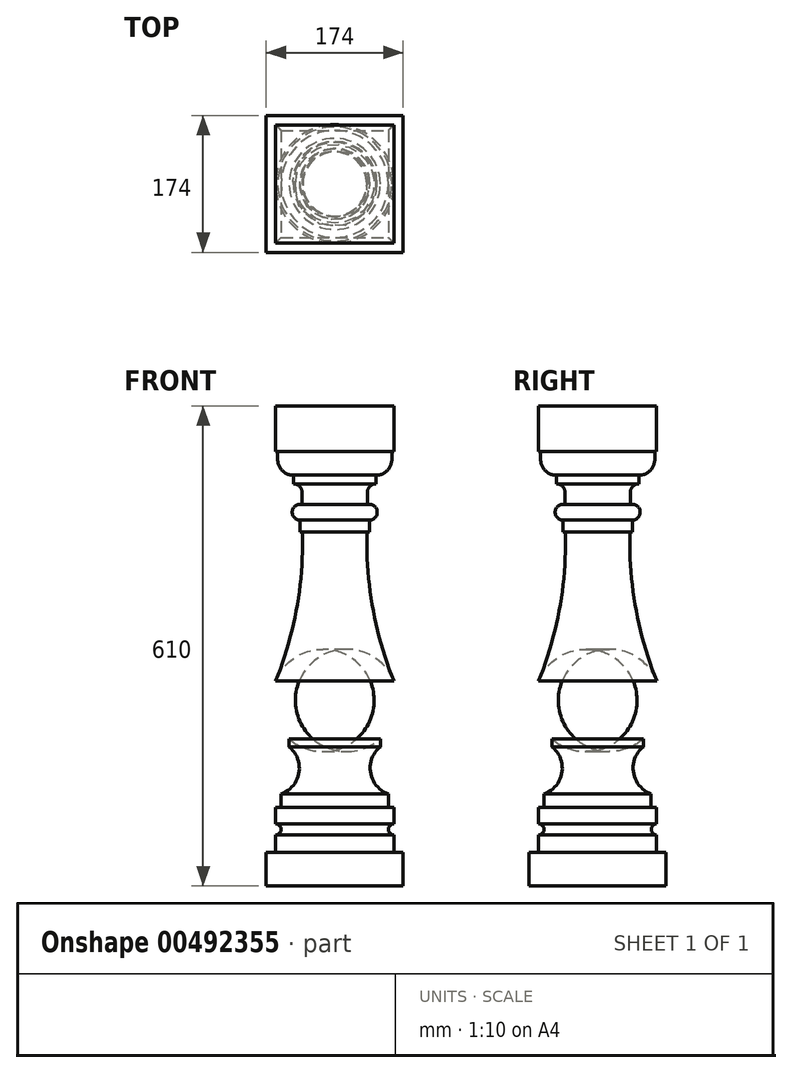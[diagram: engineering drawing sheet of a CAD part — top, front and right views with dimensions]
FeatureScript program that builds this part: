
annotation { "Feature Type Name" : "Feature", "Feature Type Description" : "" }
export const myFeature = defineFeature(function(context is Context, id is Id, definition is map)
    precondition{}
    {
        {
            var Q0;
            Q0=qCreatedBy(makeId("Top.planeOp"),FACE);
            var sketch = newSketch(context, id + "F0", { "sketchPlane" : qUnion([Q0])});
            skLineSegment(sketch, "E0.bottom", {"start": v(87, -87) * mm, "end": v(-87, -87) * mm});
            skLineSegment(sketch, "E0.top", {"start": v(87, 87) * mm, "end": v(-87, 87) * mm});
            skLineSegment(sketch, "E0.left", {"start": v(87, -87) * mm, "end": v(87, 87) * mm});
            skLineSegment(sketch, "E0.right", {"start": v(-87, -87) * mm, "end": v(-87, 87) * mm});
            skPoint(sketch, "E0.middle", {"position": v(0, 0) * mm});
            skSolve(sketch);
        }
        {
            var Q0;
            Q0 = qSketchRegion(id + "F0", true);
            extrude(context, id + "F1", {"entities" : qUnion([Q0]), "depth" : 43 * mm});
        }
        {
            var Q0;
            Q0=makeQuery(id+"F1.opExtrude","CAP_FACE",FACE,{"disambiguationData":[OSD([sQuery(id+"F0.wireOp",EDGE,"E0.bottom"),sQuery(id+"F0.wireOp",EDGE,"E0.top"),sQuery(id+"F0.wireOp",EDGE,"E0.left"),sQuery(id+"F0.wireOp",EDGE,"E0.right")])],"isStart":false});
            var sketch = newSketch(context, id + "F2", { "sketchPlane" : qUnion([Q0])});
            skLineSegment(sketch, "E1.bottom", {"start": v(75, -75) * mm, "end": v(-75, -75) * mm});
            skLineSegment(sketch, "E1.top", {"start": v(75, 75) * mm, "end": v(-75, 75) * mm});
            skLineSegment(sketch, "E1.left", {"start": v(75, -75) * mm, "end": v(75, 75) * mm});
            skLineSegment(sketch, "E1.right", {"start": v(-75, -75) * mm, "end": v(-75, 75) * mm});
            skPoint(sketch, "E1.middle", {"position": v(0, 0) * mm});
            skSolve(sketch);
        }
        {
            var Q0;
            Q0 = qSketchRegion(id + "F2", true);
            extrude(context, id + "F3", {"entities" : qUnion([Q0]), "operationType" : NewBodyOperationType.ADD, "depth" : 57 * mm});
        }
        {
            var Q0;
            Q0=makeQuery(id+"F3.opExtrude","SWEPT_FACE",FACE,{"disambiguationData":[OSD([sQuery(id+"F2.wireOp",EDGE,"E1.bottom")])]});
            var sketch = newSketch(context, id + "F4", { "sketchPlane" : qUnion([Q0])});
            skCircle(sketch, "E2", {"center": v(75, 72) * mm, "radius": 7 * mm});
            skCircle(sketch, "E3", {"center": v(-75, 72) * mm, "radius": 7 * mm});
            skSolve(sketch);
        }
        {
            var Q0;
            Q0 = qSketchRegion(id + "F4", true);
            extrude(context, id + "F5", {"entities" : qUnion([Q0]), "operationType" : NewBodyOperationType.REMOVE, "endBound" : BoundingType.THROUGH_ALL, "oppositeDirection" : true, "depth" : 123 * mm});
        }
        {
            var Q0;
            {var subQ0=sQuery(id+"F2.wireOp",EDGE,"E1.bottom");var subQ1=sQuery(id+"F2.wireOp",EDGE,"E1.left");var subQ2=sQuery(id+"F2.wireOp",EDGE,"E1.top");Q0=makeQuery(id+"F5.boolean.opBoolean","SPLIT",FACE,{"disambiguationData":[TD([makeQuery(id+"F3.opExtrude","CAP_FACE",FACE,{"disambiguationData":[OSD([subQ0,subQ2,subQ1,sQuery(id+"F2.wireOp",EDGE,"E1.right")])],"isStart":false})])],"derivedFrom":makeQuery(id+"F3.opExtrude","SWEPT_FACE",FACE,{"disambiguationData":[OSD([subQ1])]})});}
            var sketch = newSketch(context, id + "F6", { "sketchPlane" : qUnion([Q0])});
            skCircle(sketch, "E4", {"center": v(75, 72) * mm, "radius": 7 * mm});
            skCircle(sketch, "E5", {"center": v(-75, 72) * mm, "radius": 7 * mm});
            skSolve(sketch);
        }
        {
            var Q0;
            Q0 = qSketchRegion(id + "F6", true);
            extrude(context, id + "F7", {"entities" : qUnion([Q0]), "operationType" : NewBodyOperationType.REMOVE, "endBound" : BoundingType.THROUGH_ALL, "oppositeDirection" : true, "depth" : 25 * mm});
        }
        {
            var Q0;
            Q0=qCreatedBy(makeId("Front.planeOp"),FACE);
            var sketch = newSketch(context, id + "F8", { "sketchPlane" : qUnion([Q0])});
            skLineSegment(sketch, "E6", {"start": v(0, 100) * mm, "end": v(68, 100) * mm});
            skLineSegment(sketch, "E7", {"start": v(68, 100) * mm, "end": v(68, 117) * mm});
            skLineSegment(sketch, "E8", {"start": v(57.88, 177) * mm, "end": v(57.88, 187) * mm});
            skLineSegment(sketch, "E9", {"start": v(44, 450) * mm, "end": v(44, 465) * mm});
            skLineSegment(sketch, "E10", {"start": v(0, 552) * mm, "end": v(0, 100) * mm});
            skArc(sketch, "E11", {"start": v(57.88, 177) * mm, "mid": v(45.49, 144.06) * mm, "end": v(68, 117) * mm});
            skArc(sketch, "E12", {"start": v(57.88, 187) * mm, "mid": v(78.25, 220.89) * mm, "end": v(75.22, 260.32) * mm});
            skPoint(sketch, "E13.middle", {"position": v(0, 0) * mm});
            skLineSegment(sketch, "E14", {"start": v(0, 0) * mm, "end": v(113.87, 0) * mm, "construction": true});
            skLineSegment(sketch, "E15", {"start": v(80, 149.88) * mm, "end": v(45, 149.88) * mm, "construction": true});
            skLineSegment(sketch, "E16", {"start": v(15, 235.85) * mm, "end": v(80, 235.85) * mm, "construction": true});
            skLineSegment(sketch, "E17", {"start": v(44, 450) * mm, "end": v(41, 450) * mm});
            skArc(sketch, "E18", {"start": v(41, 450) * mm, "mid": v(48.24, 353.38) * mm, "end": v(75.22, 260.32) * mm});
            skArc(sketch, "E19", {"start": v(44, 465) * mm, "mid": v(54, 475) * mm, "end": v(44, 485) * mm});
            skLineSegment(sketch, "E20", {"start": v(44, 475) * mm, "end": v(54, 475) * mm, "construction": true});
            skLineSegment(sketch, "E21", {"start": v(44, 485) * mm, "end": v(41.5, 485) * mm});
            skLineSegment(sketch, "E22", {"start": v(41.5, 485) * mm, "end": v(41.5, 500) * mm});
            skLineSegment(sketch, "E23", {"start": v(52.5, 511) * mm, "end": v(52.5, 511) * mm});
            skLineSegment(sketch, "E24", {"start": v(52.5, 511) * mm, "end": v(52.5, 522) * mm});
            skLineSegment(sketch, "E25", {"start": v(52.5, 522) * mm, "end": v(52.5, 522) * mm});
            skLineSegment(sketch, "E26", {"start": v(72.5, 542) * mm, "end": v(72.5, 552) * mm});
            skLineSegment(sketch, "E27", {"start": v(72.5, 552) * mm, "end": v(0, 552) * mm});
            skPoint(sketch, "E28.visualSharp", {"position": v(41.5, 511) * mm});
            skArc(sketch, "E28.filletArc", {"start": v(52.5, 511) * mm, "mid": v(44.72, 507.78) * mm, "end": v(41.5, 500) * mm});
            skPoint(sketch, "E29.visualSharp", {"position": v(72.5, 522) * mm});
            skArc(sketch, "E29.filletArc", {"start": v(52.5, 522) * mm, "mid": v(66.64, 527.86) * mm, "end": v(72.5, 542) * mm});
            skSolve(sketch);
        }
        {
            var Q0;
            Q0=makeQuery(id+"F8.imprint","IMPRINT",FACE,{"disambiguationData":[TD([[makeQuery(id+"F8.imprint","IMPRINT",EDGE,{"derivedFrom":sQuery(id+"F8.wireOp",EDGE,"E6")}),1.0]])]});
            var Q1;
            Q1=sQuery(id+"F8.wireOp",EDGE,"E10");
            revolve(context, id + "F9", {"operationType" : NewBodyOperationType.ADD, "entities" : qUnion([Q0]), "axis" : qUnion([Q1]), "revolveType" : RevolveType.FULL});
        }
        {
            var Q0;
            Q0=makeQuery(id+"F9.opRevolve","SWEPT_FACE",FACE,{"disambiguationData":[OSD([sQuery(id+"F8.wireOp",EDGE,"E27")])]});
            var sketch = newSketch(context, id + "F10", { "sketchPlane" : qUnion([Q0])});
            skLineSegment(sketch, "E30.bottom", {"start": v(75, -75) * mm, "end": v(-75, -75) * mm});
            skLineSegment(sketch, "E30.top", {"start": v(75, 75) * mm, "end": v(-75, 75) * mm});
            skLineSegment(sketch, "E30.left", {"start": v(75, -75) * mm, "end": v(75, 75) * mm});
            skLineSegment(sketch, "E30.right", {"start": v(-75, -75) * mm, "end": v(-75, 75) * mm});
            skPoint(sketch, "E30.middle", {"position": v(0, 0) * mm});
            skSolve(sketch);
        }
        {
            var Q0;
            Q0 = qSketchRegion(id + "F10", true);
            extrude(context, id + "F11", {"entities" : qUnion([Q0]), "operationType" : NewBodyOperationType.ADD, "depth" : 58 * mm});
        }
    });
